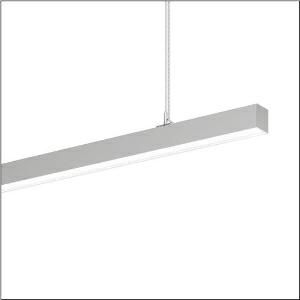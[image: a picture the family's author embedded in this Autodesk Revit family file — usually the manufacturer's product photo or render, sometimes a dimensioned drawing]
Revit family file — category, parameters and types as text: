
# Revit family: silica_r__21_51mx33dc4dsb_9471
name_source: partatom
category: Lighting Fixtures
units: mm (PartAtom-declared; Revit-internal decimal feet)

## family parameters
Cut with Voids When Loaded = No
Host = Face
Light Source = No
Part Type = Normal
Room Calculation Point = No
Round Connector Dimension = Use Diameter
Shared = No

## types (1)
- --- (1 x LED, 14790 lm, 93.9 W, 4000K)
    Apparent Load = 94 VA
    CIE Flux Codes = 78 96 99 55 100
    Color Rendering = 80
    Color Temperature = 4000K
    Default Elevation = 1800 mm
    Description = Silica® 21, office luminaire, primary optical cover: prismatic diffuser, of PMMA, CAT 2 (L<= 3000cd/m²), light emission: direct/indirect distribution, primary light characteristic: symmetric, installation type: suspended mounting, LED, rated luminous flux: 14.790lm, luminous efficacy: 158lm/W, light colour: 840, colour temperature: 4000K, with terminal, 3+2-pole, max. 2.5mm², mains connection: 220..240V, AC, 50/60Hz, rated input power: 93.9W, luminaire housing, of aluminium, metallic grey (RAL 9006), length: 3.004mm, width: 53mm, height: 53mm, protection rating (complete): IP20, insulation class (complete): insulation class I (protective earthing), certification: CE, permissible operating ambient temperature: 0..+35°C, standard: EN 50419, packaging unit: 1 piece
    Height = 53 mm
    Lamp = 1 x LED
    Lamp Light Flux = 14790 lm
    Lamp Power = 93.9 W
    Lamp count = 1
    Length = 3004 mm
    Luminous efficacy = 158 lm/W
    Manufacturer = Siteco
    ModVariant = No
    Model = 51MX33DC4DSB
    Mounting Place = Ceiling
    Mounting Type = Pendant
    Number of Poles = 1
    OnlyDefault = Yes
    Power Factor = 1
    Product Name = Silica® 21
    Product group = office luminaire | ceiling pendant
    ProductGroupID = 902
    Protection Class = Protection class I
    Protection Degree = IP 20
    RLX_Detail_Level = 1
    RLX_Emergency_Light_Flux = 0 lm
    RLX_Emergency_Type = 0
    RLX_Emergency_Type_DB = No
    RlxData = <blob elided: 23417 chars, md5=3aec18ad>
    Socket = socket
    Standby Power = 0 W
    System Light Flux = 14790 lm
    System Power = 94 W
    Type Comments = factory setting: luminous flux: 100 % | dim-lin: 254 | 323 mA
    Type Image = l_1313621.jpg
    URL = http://relux.com
    VarID = @adj_067021
    Voltage = 0 V
    Weight = 0.00 kg
    Width = 53 mm

## geometry (parser evidence)
native form markers: Blend x4, Sweep x11
no freeform markers — native parametric forms only
